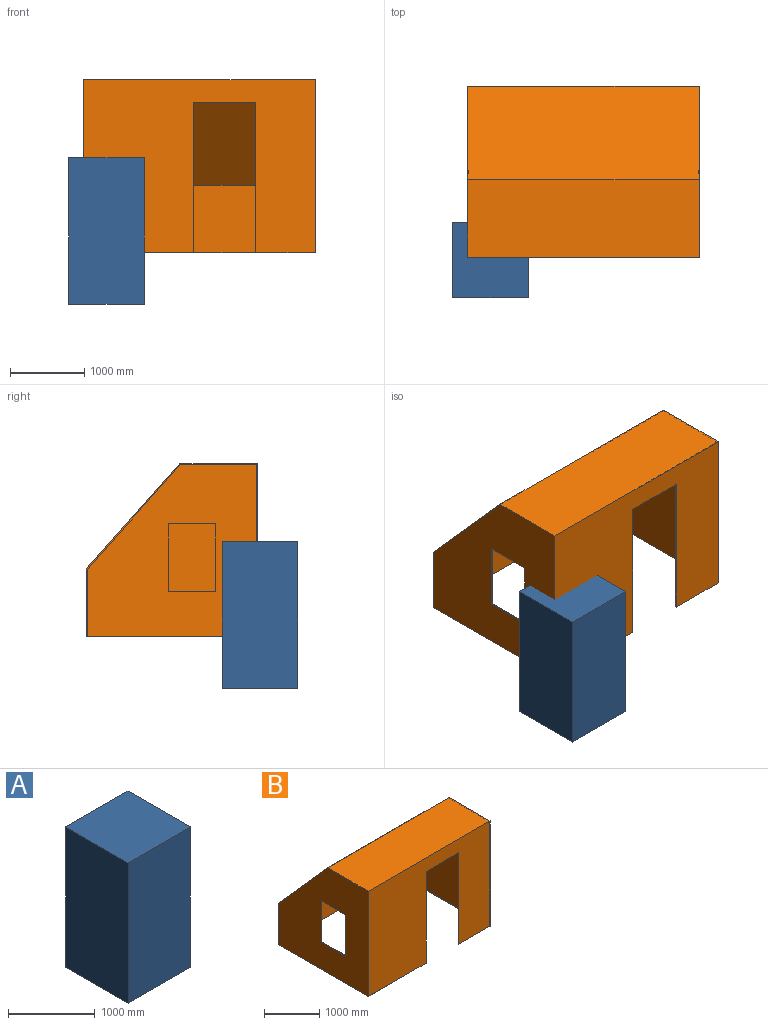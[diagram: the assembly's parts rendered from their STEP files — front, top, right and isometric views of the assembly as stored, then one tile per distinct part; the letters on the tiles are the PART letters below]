
ASSEMBLY  parts=2 mates=2
PART A: 6 faces, bbox 1016x1016x1981.2 mm
  f0: plane 1981.2x1016mm, normal (0,1,0), area 2012899.2mm2, adj f1,f3,f4,f5
  f1: plane 1981.2x1016mm, normal (-1,0,0), area 2012899.2mm2, adj f0,f2,f4,f5
  f2: plane 1981.2x1016mm, normal (0,-1,0), area 2012899.2mm2, adj f1,f3,f4,f5
  f3: plane 1981.2x1016mm, normal (1,0,0), area 2012899.2mm2, adj f0,f2,f4,f5
  f4: plane 1016x1016mm, normal (0,0,1), area 1032256mm2, adj f0,f1,f2,f3
  f5: plane 1016x1016mm, normal (0,0,-1), area 1032256mm2, adj f0,f1,f2,f3
PART B: 20 faces, bbox 3124.2x2311.4x2336.8 mm
  f0: plane 2336.8x2311.4mm, normal (-1,0,0), area 3921425.8mm2, adj f3,f4,f6,f7,f8,f16,f17,f18
  f1: plane 2324.1x2286mm, normal (1,0,0), area 3842963.7mm2, adj f2,f3,f9,f11,f12,f16,f17,f18
  f2: plane 3098.8x2324.1mm, normal (0,1,0), area 5498698.7mm2, adj f1,f3,f10,f11,f13,f14,f15
  f3: plane 3124.2x2311.4mm, normal (0,0,-1), area 126773.9mm2, adj f0,f1,f2,f4,f5,f6,f9,f10
  f4: plane 3124.2x914.4mm, normal (0,1,0), area 2856768.5mm2, adj f0,f3,f5,f8
  f5: plane 2336.8x2311.4mm, normal (1,0,0), area 4502069.8mm2, adj f3,f4,f6,f7,f8
  f6: plane 3124.2x2336.8mm, normal (0,-1,0), area 5597408.2mm2, adj f0,f3,f5,f7,f13,f14,f15
  f7: plane 3124.2x1047.04mm, normal (0,0,1), area 3271176.3mm2, adj f0,f5,f6,f8
  f8: plane 3124.2x1422.4mm, normal (0,0.75,0.66), area 5945687.3mm2, adj f0,f4,f5,f7
  f9: plane 3098.8x909.57mm, normal (0,-1,0), area 2818580.1mm2, adj f1,f3,f10,f12
  f10: plane 2324.1x2286mm, normal (-1,0,0), area 4423607.7mm2, adj f2,f3,f9,f11,f12
  f11: plane 3098.8x1028.64mm, normal (0,0,-1), area 3187553.7mm2, adj f1,f2,f10,f12
  f12: plane 3098.8x1414.53mm, normal (0,-0.75,-0.66), area 5864712.8mm2, adj f1,f9,f10,f11
  f13: plane 2032x12.7mm, normal (1,0,0), area 25806.4mm2, adj f2,f3,f6,f15
  f14: plane 2032x12.7mm, normal (-1,0,0), area 25806.4mm2, adj f2,f3,f6,f15
  f15: plane 838.2x12.7mm, normal (0,0,-1), area 10645.1mm2, adj f2,f6,f13,f14
  f16: plane 635x12.7mm, normal (0,0,-1), area 8064.5mm2, adj f0,f1,f17,f19
  f17: plane 914.4x12.7mm, normal (0,-1,0), area 11612.9mm2, adj f0,f1,f16,f18
  f18: plane 635x12.7mm, normal (0,0,1), area 8064.5mm2, adj f0,f1,f17,f19
  f19: plane 914.4x12.7mm, normal (0,1,0), area 11612.9mm2, adj f0,f1,f16,f18
PLACE A t=(-837.01,-370.72,-347.36)mm
PLACE B t=(418.63,820.77,349.89)mm
MATE parallel A.f2 <-> B.f2  axis (0,-1,0) through (-837.01,-878.72,643.24)mm
MATE parallel A.f5 <-> B.f3  axis (0,0,-1) through (-837.01,-370.72,-347.36)mm
